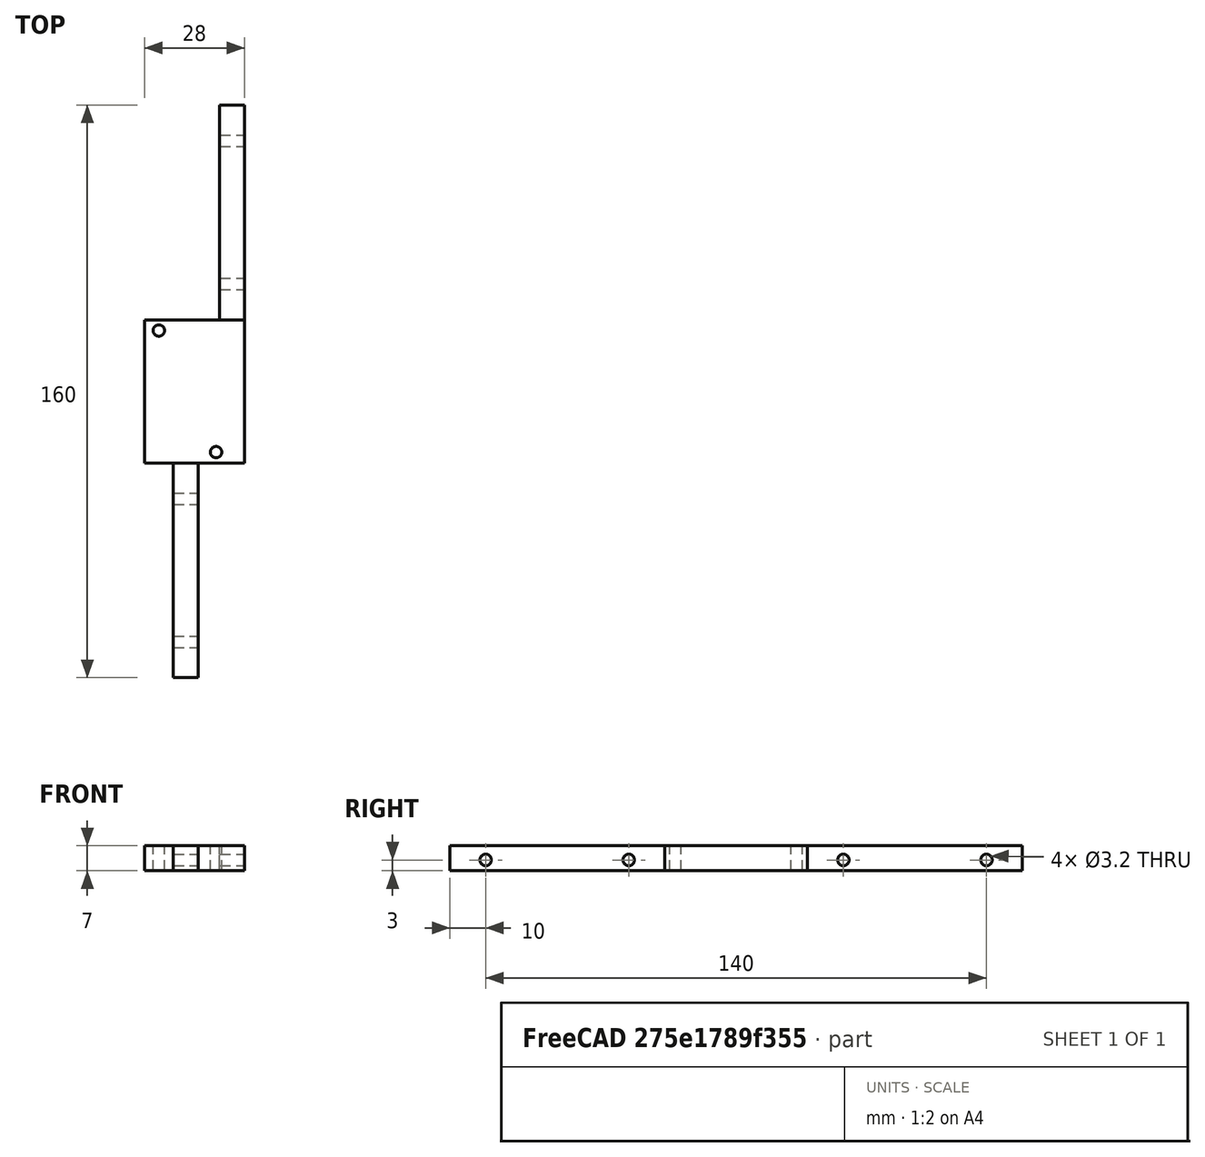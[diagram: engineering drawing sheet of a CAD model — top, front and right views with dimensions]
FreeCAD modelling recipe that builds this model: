
FCSTD DOCUMENT  (FreeCAD 0.15R4671 (Git))
Label: liaison_supports
License: All rights reserved
LicenseURL: http://fr.wikipedia.org/wiki/<copyright redacted>
objects: Part::Cylinder×6, Part::Cut×6, Part::Box×3
note: 15 computed .brp shape members not serialized (recipe doc carries the construction recipe); baked Part::Feature solids carry a one-line shape summary decoded from their .brp

FEATURE [Part::Box] Box  label="Cube007"
  Height = 7
  Length = 60
  Placement = pos=(0,0,0) rot=(0,0,1;1.5708rad)
  Width = 7
FEATURE [Part::Cylinder] Cylinder  label="Cylindre010"
  Angle = 360
  Height = 20
  Placement = pos=(-12,10,3) rot=(0,1,0;1.5708rad)
  Radius = 1.6
FEATURE [Part::Cylinder] Cylinder001  label="Cylindre011"
  Angle = 360
  Height = 20
  Placement = pos=(-12,50,3) rot=(0,1,0;1.5708rad)
  Radius = 1.6
FEATURE [Part::Box] Box001  label="Cube008"
  Height = 7
  Length = 40
  Placement = pos=(0,-40,0) rot=(0,0,1;1.5708rad)
  Width = 28
FEATURE [Part::Box] Box002  label="Cube009"
  Height = 7
  Length = 60
  Placement = pos=(-13,-100,0) rot=(0,0,1;1.5708rad)
  Width = 7
FEATURE [Part::Cylinder] Cylinder002  label="Cylindre012"
  Angle = 360
  Height = 20
  Placement = pos=(-20,-90,3) rot=(0,1,0;1.5708rad)
  Radius = 1.6
FEATURE [Part::Cylinder] Cylinder003  label="Cylindre013"
  Angle = 360
  Height = 20
  Placement = pos=(-20,-50,3) rot=(0,1,0;1.5708rad)
  Radius = 1.6
FEATURE [Part::Cylinder] Cylinder004  label="Cylindre014"
  Angle = 360
  Height = 20
  Placement = pos=(-8,-37,-9) rot=(0,0,1;0rad)
  Radius = 1.6
FEATURE [Part::Cylinder] Cylinder005  label="Cylindre015"
  Angle = 360
  Height = 20
  Placement = pos=(-24,-3,-9) rot=(0,0,1;0rad)
  Radius = 1.6
FEATURE [Part::Cut] Cut
  Base = -> Box
  Tool = -> Cylinder
FEATURE [Part::Cut] Cut001
  Base = -> Cut
  Tool = -> Cylinder001
FEATURE [Part::Cut] Cut002
  Base = -> Box002
  Tool = -> Cylinder002
FEATURE [Part::Cut] Cut003
  Base = -> Cut002
  Tool = -> Cylinder003
FEATURE [Part::Cut] Cut004
  Base = -> Box001
  Tool = -> Cylinder004
FEATURE [Part::Cut] Cut005
  Base = -> Cut004
  Tool = -> Cylinder005
